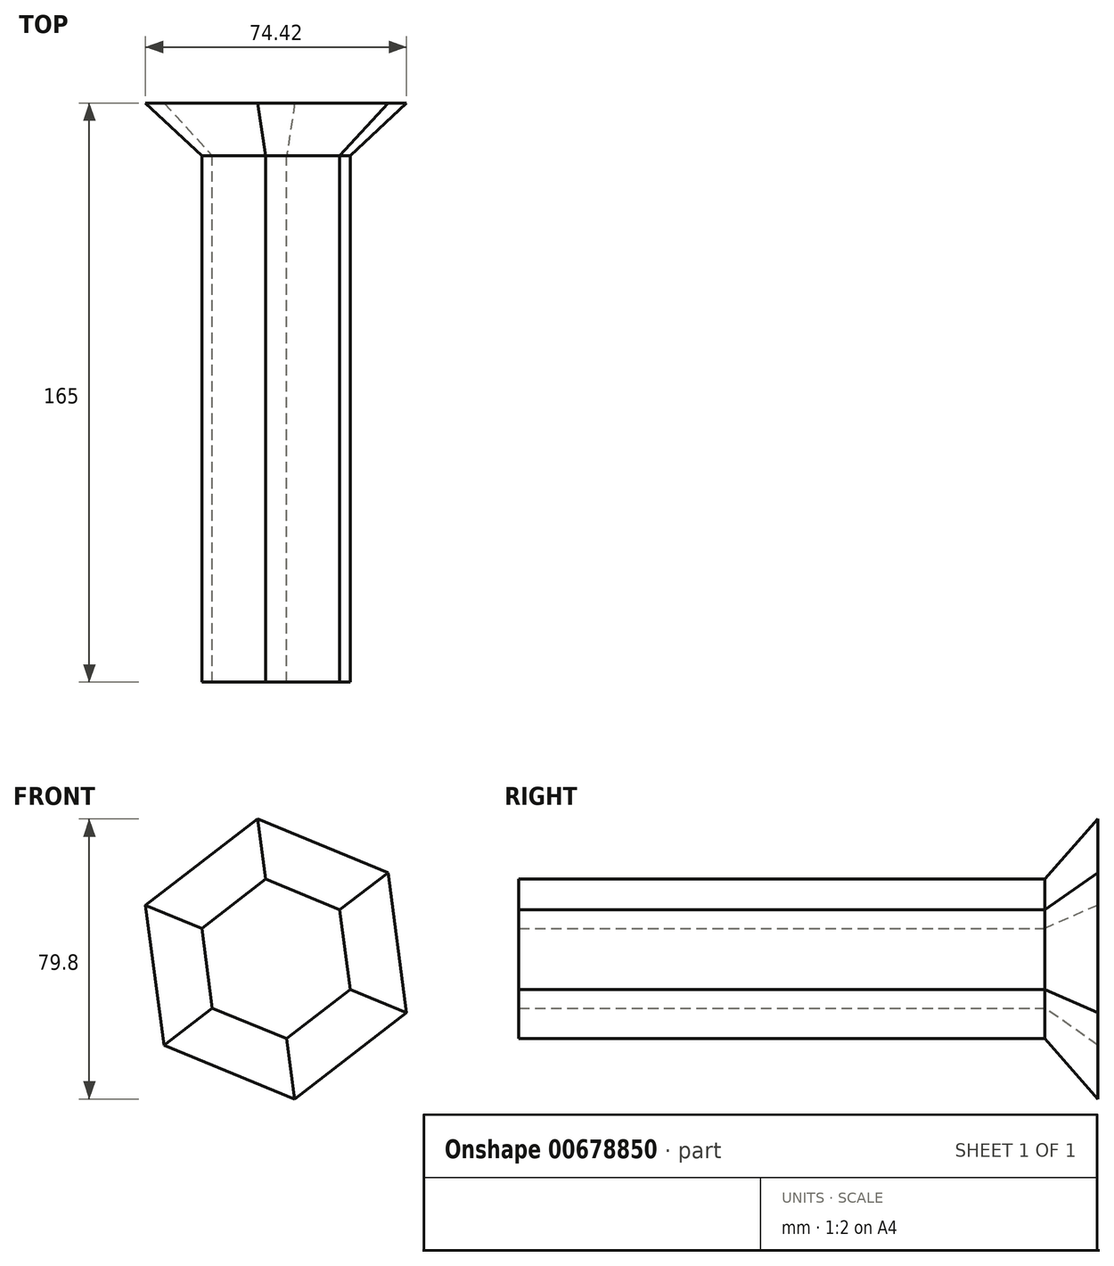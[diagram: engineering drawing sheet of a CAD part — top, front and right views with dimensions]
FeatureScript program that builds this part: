
annotation { "Feature Type Name" : "Feature", "Feature Type Description" : "" }
export const myFeature = defineFeature(function(context is Context, id is Id, definition is map)
    precondition{}
    {
        {
            var Q0;
            Q0=qCreatedBy(makeId("Front.planeOp"),FACE);
            var sketch = newSketch(context, id + "F0", { "sketchPlane" : qUnion([Q0])});
            skLineSegment(sketch, "E0.0", {"start": v(-3.02, 22.73) * mm, "end": v(18.17, 13.98) * mm});
            skLineSegment(sketch, "E0.1", {"start": v(18.17, 13.98) * mm, "end": v(21.2, -8.75) * mm});
            skLineSegment(sketch, "E0.2", {"start": v(21.2, -8.75) * mm, "end": v(3.02, -22.73) * mm});
            skLineSegment(sketch, "E0.3", {"start": v(3.02, -22.73) * mm, "end": v(-18.17, -13.98) * mm});
            skLineSegment(sketch, "E0.4", {"start": v(-18.17, -13.98) * mm, "end": v(-21.2, 8.75) * mm});
            skLineSegment(sketch, "E0.5", {"start": v(-21.2, 8.75) * mm, "end": v(-3.02, 22.73) * mm});
            skSolve(sketch);
        }
        {
            var Q0;
            Q0=makeQuery(id+"F0.imprint","IMPRINT",FACE,{"disambiguationData":[TD([[makeQuery(id+"F0.imprint","IMPRINT",EDGE,{"derivedFrom":sQuery(id+"F0.wireOp",EDGE,"E0.0")}),-1.0]])]});
            var Q1;
            Q1=sQuery(id+"F0.wireOp",EDGE,"E0.0");
            var Q2;
            Q2=sQuery(id+"F0.wireOp",EDGE,"E0.1");
            var Q3;
            Q3=sQuery(id+"F0.wireOp",EDGE,"E0.2");
            var Q4;
            Q4=sQuery(id+"F0.wireOp",EDGE,"E0.3");
            var Q5;
            Q5=sQuery(id+"F0.wireOp",EDGE,"E0.4");
            var Q6;
            Q6=sQuery(id+"F0.wireOp",EDGE,"E0.5");
            extrude(context, id + "F1", {"entities" : qUnion([Q0]), "surfaceEntities" : qUnion([Q1, Q2, Q3, Q4, Q5, Q6]), "depth" : 150 * mm, "offsetDistance" : 25 * mm});
        }
        {
            var Q0;
            Q0=makeQuery(id+"F1.opExtrude","CAP_FACE",FACE,{"disambiguationData":[OSD([sQuery(id+"F0.wireOp",EDGE,"E0.0"),sQuery(id+"F0.wireOp",EDGE,"E0.1"),sQuery(id+"F0.wireOp",EDGE,"E0.2"),sQuery(id+"F0.wireOp",EDGE,"E0.3"),sQuery(id+"F0.wireOp",EDGE,"E0.4"),sQuery(id+"F0.wireOp",EDGE,"E0.5")])],"isStart":true});
            extrude(context, id + "F2", {"entities" : qUnion([Q0]), "operationType" : NewBodyOperationType.ADD, "depth" : 15 * mm, "offsetDistance" : 25 * mm, "hasDraft" : true, "draftAngle" : 45 * degree});
        }
    });
